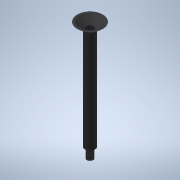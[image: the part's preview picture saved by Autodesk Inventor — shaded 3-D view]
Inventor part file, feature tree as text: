
AUTODESK INVENTOR PART (.ipt)
format: ipt  version: 2021.3 (Build 253353000, 353)  size: 124,416 bytes
history: native  units: mm
features: revolve x1, thread x1, shell x1, sketch x1
ambient origin geometry x8: Origin, YZ Plane, XZ Plane, XY Plane, X Axis, Y Axis, Z Axis, Center Point
bodies: Volumenkörper1 (feature_tree)
feature tree (4):
  revolve  "Umdrehung1"
  thread  "Gewinde1"  [1 undecoded]
  shell  "Wandung4"  Thickness=0.0mm
  sketch  "Skizze1"  dims[d2=7.0mm d4=0.5mm d5=0.5mm d6=2.0mm d7=4.0mm d14=90.0deg d23=6.981317mm d24=5.0mm d25=85.0mm d26=6.5mm d27=0.0mm d31=1.0mm]
note: 1 required parameter value undecoded (feature->parameter linkage not recoverable at this tier; creation-order binding heuristic only, values carry confidence <= 0.55)
